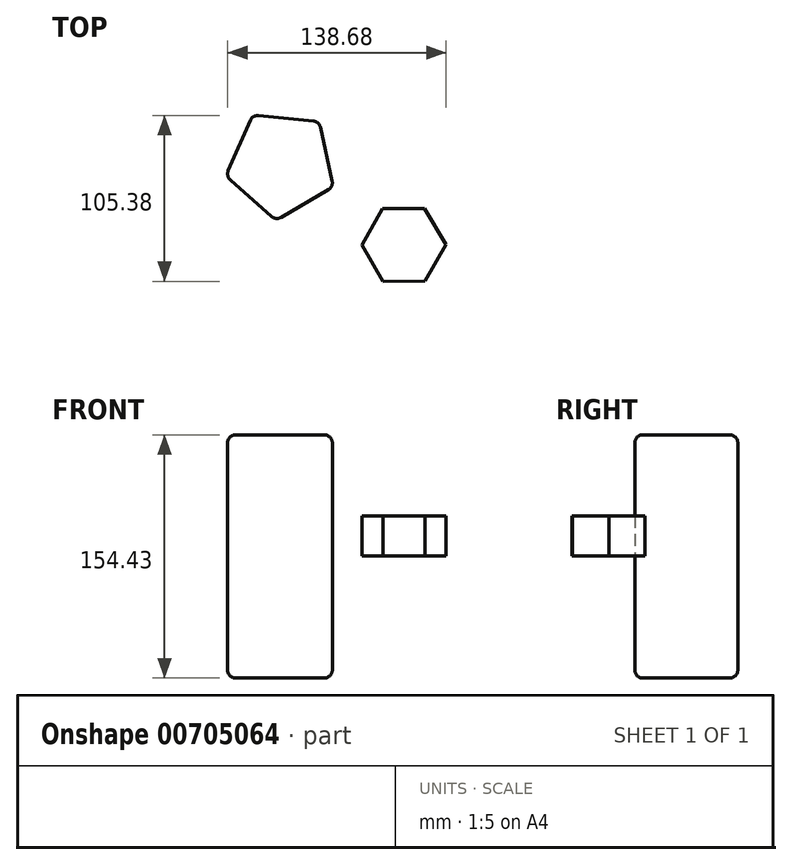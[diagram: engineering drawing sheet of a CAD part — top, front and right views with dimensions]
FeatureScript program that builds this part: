
annotation { "Feature Type Name" : "Feature", "Feature Type Description" : "" }
export const myFeature = defineFeature(function(context is Context, id is Id, definition is map)
    precondition{}
    {
        {
            var Q0;
            Q0=qCreatedBy(makeId("Top.planeOp"),FACE);
            var sketch = newSketch(context, id + "F0", { "sketchPlane" : qUnion([Q0])});
            skCircle(sketch, "E0.cCircle", {"center": v(-38.55, 7.3) * mm, "radius": 29.16 * mm, "construction": true});
            skLineSegment(sketch, "E0.0", {"start": v(-5.53, -7.15) * mm, "end": v(-42.1, -28.56) * mm});
            skLineSegment(sketch, "E0.1", {"start": v(-42.1, -28.56) * mm, "end": v(-73.76, -0.41) * mm});
            skLineSegment(sketch, "E0.2", {"start": v(-73.76, -0.41) * mm, "end": v(-56.77, 38.4) * mm});
            skLineSegment(sketch, "E0.3", {"start": v(-56.77, 38.4) * mm, "end": v(-14.6, 34.25) * mm});
            skLineSegment(sketch, "E0.4", {"start": v(-14.6, 34.25) * mm, "end": v(-5.53, -7.15) * mm});
            skPoint(sketch, "E0.0.midPoint", {"position": v(-23.8, -17.86) * mm});
            skSolve(sketch);
        }
        {
            var Q0;
            Q0=makeQuery(id+"F0.imprint","IMPRINT",FACE,{"disambiguationData":[TD([[makeQuery(id+"F0.imprint","IMPRINT",EDGE,{"derivedFrom":sQuery(id+"F0.wireOp",EDGE,"E0.0")}),-1.0]])]});
            extrude(context, id + "F1", {"entities" : qUnion([Q0]), "depth" : 76.96 * mm, "offsetDistance" : 25.4 * mm, "hasSecondDirection" : true, "secondDirectionOppositeDirection" : true, "secondDirectionDepth" : 77.47 * mm});
        }
        {
            var Q0;
            Q0=makeQuery(id+"F1.opExtrude","SWEPT_FACE",FACE,{"disambiguationData":[OSD([sQuery(id+"F0.wireOp",EDGE,"E0.1")])]});
            var Q1;
            Q1=makeQuery(id+"F1.opExtrude","SWEPT_FACE",FACE,{"disambiguationData":[OSD([sQuery(id+"F0.wireOp",EDGE,"E0.2")])]});
            var Q2;
            Q2=makeQuery(id+"F1.opExtrude","SWEPT_FACE",FACE,{"disambiguationData":[OSD([sQuery(id+"F0.wireOp",EDGE,"E0.3")])]});
            var Q3;
            Q3=makeQuery(id+"F1.opExtrude","SWEPT_FACE",FACE,{"disambiguationData":[OSD([sQuery(id+"F0.wireOp",EDGE,"E0.4")])]});
            var Q4;
            Q4=makeQuery(id+"F1.opExtrude","SWEPT_FACE",FACE,{"disambiguationData":[OSD([sQuery(id+"F0.wireOp",EDGE,"E0.0")])]});
            fillet(context, id + "F2", {"entities" : qUnion([Q0, Q1, Q2, Q3, Q4]), "radius" : 5.08 * mm, "tangentPropagation" : true, "allowEdgeOverflow" : false});
        }
        {
            var Q0;
            Q0=qCreatedBy(makeId("Top.planeOp"),FACE);
            var sketch = newSketch(context, id + "F3", { "sketchPlane" : qUnion([Q0])});
            skCircle(sketch, "E1.cCircle", {"center": v(39.3, -44.1) * mm, "radius": 26.67 * mm, "construction": true});
            skLineSegment(sketch, "E1.0", {"start": v(52.81, -67.1) * mm, "end": v(26.14, -67.31) * mm});
            skLineSegment(sketch, "E1.1", {"start": v(26.14, -67.31) * mm, "end": v(12.62, -44.32) * mm});
            skLineSegment(sketch, "E1.2", {"start": v(12.62, -44.32) * mm, "end": v(25.78, -21.11) * mm});
            skLineSegment(sketch, "E1.3", {"start": v(25.78, -21.11) * mm, "end": v(52.45, -20.9) * mm});
            skLineSegment(sketch, "E1.4", {"start": v(52.45, -20.9) * mm, "end": v(65.97, -43.9) * mm});
            skLineSegment(sketch, "E1.5", {"start": v(65.97, -43.9) * mm, "end": v(52.81, -67.1) * mm});
            skSolve(sketch);
        }
        {
            var Q0;
            Q0 = qSketchRegion(id + "F3", true);
            extrude(context, id + "F4", {"entities" : qUnion([Q0]), "depth" : 25.4 * mm, "offsetDistance" : 25.4 * mm});
        }
        {
            var Q0;
            Q0 = qSketchRegion(id + "F3", true);
            extrude(context, id + "F5", {"entities" : qUnion([Q0]), "operationType" : NewBodyOperationType.ADD, "depth" : 25.4 * mm, "offsetDistance" : 25.4 * mm});
        }
    });
